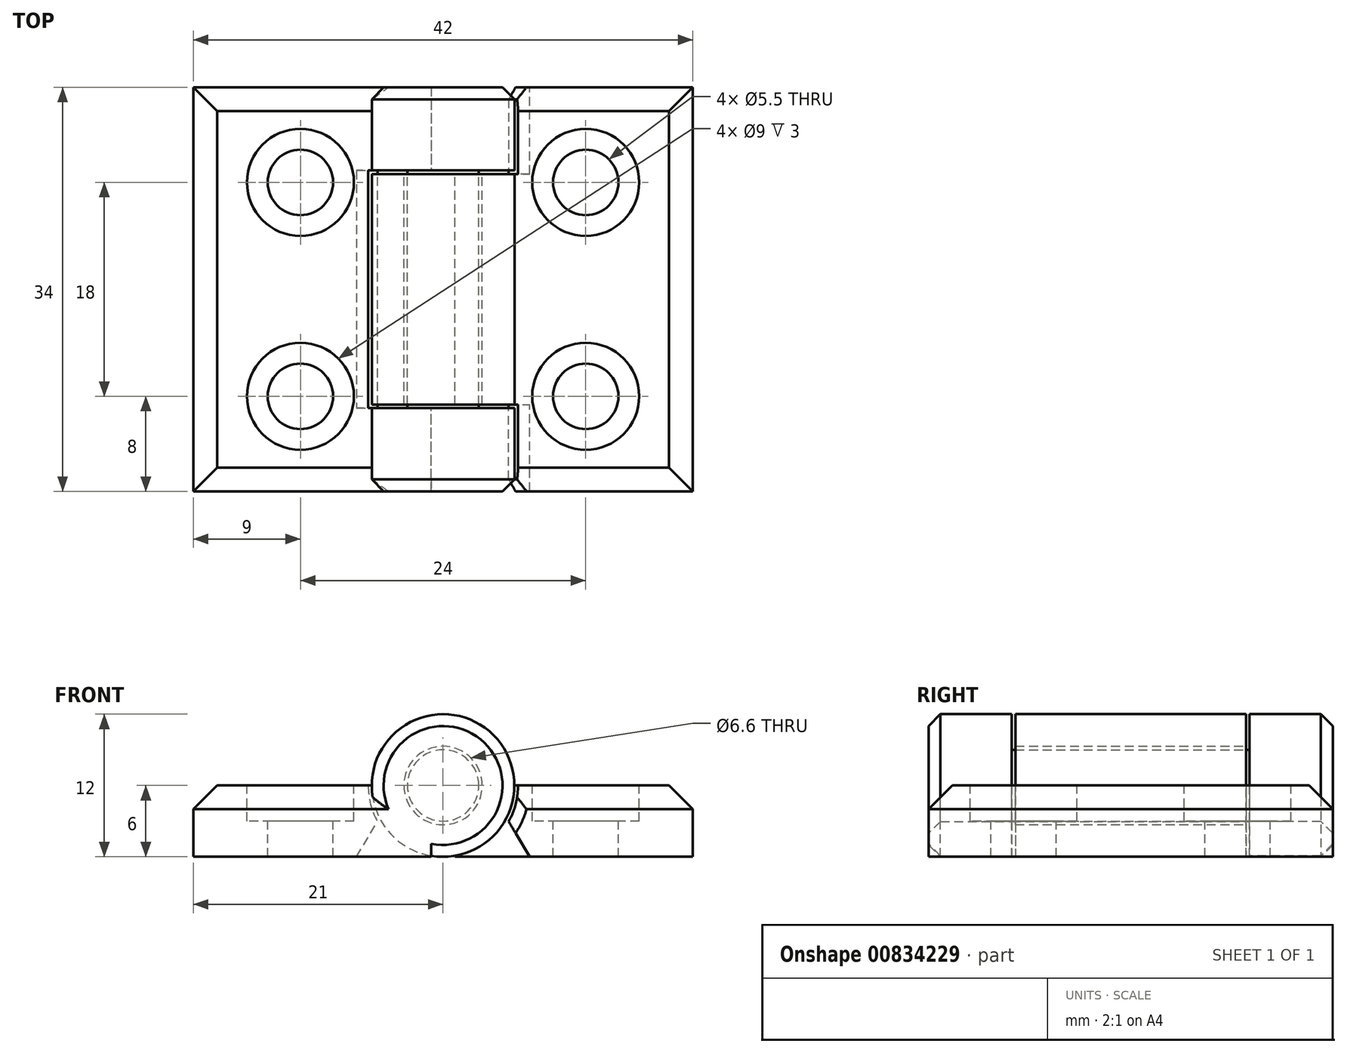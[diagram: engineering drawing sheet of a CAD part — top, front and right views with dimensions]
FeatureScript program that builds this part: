
annotation { "Feature Type Name" : "Feature", "Feature Type Description" : "" }
export const myFeature = defineFeature(function(context is Context, id is Id, definition is map)
    precondition{}
    {
        {
            var Q0;
            Q0=qCreatedBy(makeId("Front.planeOp"),FACE);
            var sketch = newSketch(context, id + "F0", { "sketchPlane" : qUnion([Q0])});
            skLineSegment(sketch, "E0.bottom", {"start": v(0, 0) * mm, "end": v(20, 0) * mm});
            skLineSegment(sketch, "E0.top", {"start": v(0, 6) * mm, "end": v(20, 6) * mm});
            skLineSegment(sketch, "E0.left", {"start": v(0, 0) * mm, "end": v(0, 6) * mm});
            skLineSegment(sketch, "E0.right", {"start": v(20, 0) * mm, "end": v(20, 6) * mm});
            skLineSegment(sketch, "E1.bottom", {"start": v(22, 6) * mm, "end": v(42, 6) * mm});
            skLineSegment(sketch, "E1.top", {"start": v(22, 0) * mm, "end": v(42, 0) * mm});
            skLineSegment(sketch, "E1.left", {"start": v(22, 6) * mm, "end": v(22, 0) * mm});
            skLineSegment(sketch, "E1.right", {"start": v(42, 6) * mm, "end": v(42, 0) * mm});
            skLineSegment(sketch, "E2", {"start": v(20, 6) * mm, "end": v(22, 6) * mm, "construction": true});
            skCircle(sketch, "E3", {"center": v(21, 6) * mm, "radius": 6 * mm});
            skCircle(sketch, "E4", {"center": v(21, 6) * mm, "radius": 3.3 * mm});
            skCircle(sketch, "E5", {"center": v(21, 6) * mm, "radius": 3 * mm});
            skCircle(sketch, "E6", {"center": v(21, 6) * mm, "radius": 6.3 * mm});
            skSolve(sketch);
        }
        {
            var Q0;
            {var subQ0=sQuery(id+"F0.wireOp",EDGE,"E0.left");Q0=makeQuery(id+"F0.imprint","IMPRINT",FACE,{"disambiguationData":[TD([[makeQuery(id+"F0.imprint","IMPRINT",EDGE,{"derivedFrom":subQ0}),-1.0]])]});}
            var Q1;
            {var subQ0=sQuery(id+"F0.wireOp",EDGE,"E1.right");Q1=makeQuery(id+"F0.imprint","IMPRINT",FACE,{"disambiguationData":[TD([[makeQuery(id+"F0.imprint","IMPRINT",EDGE,{"derivedFrom":subQ0}),-1.0]])]});}
            var Q2;
            {var subQ1=sQuery(id+"F0.wireOp",EDGE,"E1.bottom");var subQ7=sQuery(id+"F0.wireOp",EDGE,"E6");var subQ9=makeQuery(id+"F0.imprint","INTERSECT",VERTEX,{"derivedFrom":[subQ1,subQ7]});Q2=makeQuery(id+"F0.imprint","IMPRINT",FACE,{"disambiguationData":[TD([[makeQuery(id+"F0.imprint","IMPRINT",EDGE,{"disambiguationData":[TD([[subQ9,1.0]])],"derivedFrom":subQ1}),-1.0]])]});}
            var Q3;
            {var subQ0=sQuery(id+"F0.wireOp",EDGE,"E3");var subQ1=sQuery(id+"F0.wireOp",EDGE,"E0.top");var subQ2=makeQuery(id+"F0.imprint","INTERSECT",VERTEX,{"derivedFrom":[subQ1,subQ0]});Q3=makeQuery(id+"F0.imprint","IMPRINT",FACE,{"disambiguationData":[TD([[makeQuery(id+"F0.imprint","IMPRINT",EDGE,{"disambiguationData":[TD([[subQ2,-1.0]])],"derivedFrom":subQ1}),-1.0]])]});}
            var Q4;
            {var subQ0=sQuery(id+"F0.wireOp",EDGE,"E3");var subQ1=sQuery(id+"F0.wireOp",EDGE,"E0.right");var subQ2=makeQuery(id+"F0.imprint","INTERSECT",VERTEX,{"derivedFrom":[subQ1,subQ0]});Q4=makeQuery(id+"F0.imprint","IMPRINT",FACE,{"disambiguationData":[TD([[makeQuery(id+"F0.imprint","IMPRINT",EDGE,{"disambiguationData":[TD([[subQ2,-1.0]])],"derivedFrom":subQ1}),-1.0]])]});}
            var Q5;
            {var subQ0=sQuery(id+"F0.wireOp",EDGE,"E4");var subQ1=sQuery(id+"F0.wireOp",EDGE,"E1.bottom");var subQ2=makeQuery(id+"F0.imprint","INTERSECT",VERTEX,{"derivedFrom":[subQ1,subQ0]});Q5=makeQuery(id+"F0.imprint","IMPRINT",FACE,{"disambiguationData":[TD([[makeQuery(id+"F0.imprint","IMPRINT",EDGE,{"disambiguationData":[TD([[subQ2,-1.0]])],"derivedFrom":subQ1}),-1.0]])]});}
            var Q6;
            {var subQ0=sQuery(id+"F0.wireOp",EDGE,"E3");var subQ1=sQuery(id+"F0.wireOp",EDGE,"E0.top");var subQ2=makeQuery(id+"F0.imprint","INTERSECT",VERTEX,{"derivedFrom":[subQ1,subQ0]});Q6=makeQuery(id+"F0.imprint","IMPRINT",FACE,{"disambiguationData":[TD([[makeQuery(id+"F0.imprint","IMPRINT",EDGE,{"disambiguationData":[TD([[subQ2,-1.0]])],"derivedFrom":subQ1}),1.0]])]});}
            var Q7;
            {var subQ0=sQuery(id+"F0.wireOp",EDGE,"E0.right");var subQ1=sQuery(id+"F0.wireOp",EDGE,"E0.top");var subQ2=makeQuery(id+"F0.imprint","INTERSECT",VERTEX,{"derivedFrom":[subQ1,subQ0]});Q7=makeQuery(id+"F0.imprint","IMPRINT",FACE,{"disambiguationData":[TD([[makeQuery(id+"F0.imprint","IMPRINT",EDGE,{"disambiguationData":[TD([[subQ2,1.0]])],"derivedFrom":subQ1}),-1.0]])]});}
            var Q8;
            {var subQ6=sQuery(id+"F0.wireOp",EDGE,"E0.right");var subQ8=sQuery(id+"F0.wireOp",EDGE,"E0.top");var subQ9=makeQuery(id+"F0.imprint","INTERSECT",VERTEX,{"derivedFrom":[subQ8,subQ6]});Q8=makeQuery(id+"F0.imprint","IMPRINT",FACE,{"disambiguationData":[TD([[makeQuery(id+"F0.imprint","IMPRINT",EDGE,{"disambiguationData":[TD([[subQ9,1.0]])],"derivedFrom":subQ8}),1.0]])]});}
            var Q9;
            {var subQ0=sQuery(id+"F0.wireOp",EDGE,"E1.left");var subQ1=sQuery(id+"F0.wireOp",EDGE,"E1.bottom");var subQ2=makeQuery(id+"F0.imprint","INTERSECT",VERTEX,{"derivedFrom":[subQ1,subQ0]});Q9=makeQuery(id+"F0.imprint","IMPRINT",FACE,{"disambiguationData":[TD([[makeQuery(id+"F0.imprint","IMPRINT",EDGE,{"disambiguationData":[TD([[subQ2,-1.0]])],"derivedFrom":subQ1}),-1.0]])]});}
            extrude(context, id + "F1", {"entities" : qUnion([Q0, Q1, Q2, Q3, Q4, Q5, Q6, Q7, Q8, Q9]), "endBound" : BoundingType.SYMMETRIC, "depth" : 19.4 * mm, "offsetDistance" : 25 * mm});
        }
        {
            var Q0;
            Q0=makeQuery(id+"F1.opExtrude","CAP_FACE",FACE,{"disambiguationData":[OSD([sQuery(id+"F0.wireOp",EDGE,"E0.bottom"),sQuery(id+"F0.wireOp",EDGE,"E0.top"),sQuery(id+"F0.wireOp",EDGE,"E0.left"),sQuery(id+"F0.wireOp",EDGE,"E6")])],"isStart":false});
            var sketch = newSketch(context, id + "F2", { "sketchPlane" : qUnion([Q0])});
            skLineSegment(sketch, "E7.bottom", {"start": v(0, 0) * mm, "end": v(20, 0) * mm});
            skLineSegment(sketch, "E7.top", {"start": v(0, 6) * mm, "end": v(20, 6) * mm});
            skLineSegment(sketch, "E7.left", {"start": v(0, 0) * mm, "end": v(0, 6) * mm});
            skLineSegment(sketch, "E7.right", {"start": v(20, 0) * mm, "end": v(20, 6) * mm});
            skLineSegment(sketch, "E8.bottom", {"start": v(22, 6) * mm, "end": v(42, 6) * mm});
            skLineSegment(sketch, "E8.top", {"start": v(22, 0) * mm, "end": v(42, 0) * mm});
            skLineSegment(sketch, "E8.left", {"start": v(22, 6) * mm, "end": v(22, 0) * mm});
            skLineSegment(sketch, "E8.right", {"start": v(42, 6) * mm, "end": v(42, 0) * mm});
            skLineSegment(sketch, "E9", {"start": v(20, 6) * mm, "end": v(22, 6) * mm, "construction": true});
            skCircle(sketch, "E10", {"center": v(21, 6) * mm, "radius": 6 * mm});
            skCircle(sketch, "E11", {"center": v(21, 6) * mm, "radius": 3.3 * mm});
            skCircle(sketch, "E12", {"center": v(21, 6) * mm, "radius": 3 * mm});
            skCircle(sketch, "E13", {"center": v(21, 6) * mm, "radius": 6.3 * mm});
            skSolve(sketch);
        }
        {
            var Q0;
            {var subQ0=sQuery(id+"F2.wireOp",EDGE,"E7.left");Q0=makeQuery(id+"F2.imprint","IMPRINT",FACE,{"disambiguationData":[TD([[makeQuery(id+"F2.imprint","IMPRINT",EDGE,{"derivedFrom":subQ0}),-1.0]])]});}
            var Q1;
            {var subQ6=sQuery(id+"F2.wireOp",EDGE,"E7.right");var subQ8=sQuery(id+"F2.wireOp",EDGE,"E7.top");var subQ9=makeQuery(id+"F2.imprint","INTERSECT",VERTEX,{"derivedFrom":[subQ8,subQ6]});Q1=makeQuery(id+"F2.imprint","IMPRINT",FACE,{"disambiguationData":[TD([[makeQuery(id+"F2.imprint","IMPRINT",EDGE,{"disambiguationData":[TD([[subQ9,1.0]])],"derivedFrom":subQ8}),1.0]])]});}
            var Q2;
            {var subQ0=sQuery(id+"F2.wireOp",EDGE,"E7.right");var subQ1=sQuery(id+"F2.wireOp",EDGE,"E7.top");var subQ2=makeQuery(id+"F2.imprint","INTERSECT",VERTEX,{"derivedFrom":[subQ1,subQ0]});Q2=makeQuery(id+"F2.imprint","IMPRINT",FACE,{"disambiguationData":[TD([[makeQuery(id+"F2.imprint","IMPRINT",EDGE,{"disambiguationData":[TD([[subQ2,1.0]])],"derivedFrom":subQ1}),-1.0]])]});}
            var Q3;
            {var subQ0=sQuery(id+"F2.wireOp",EDGE,"E8.left");var subQ1=sQuery(id+"F2.wireOp",EDGE,"E8.bottom");var subQ2=makeQuery(id+"F2.imprint","INTERSECT",VERTEX,{"derivedFrom":[subQ1,subQ0]});Q3=makeQuery(id+"F2.imprint","IMPRINT",FACE,{"disambiguationData":[TD([[makeQuery(id+"F2.imprint","IMPRINT",EDGE,{"disambiguationData":[TD([[subQ2,-1.0]])],"derivedFrom":subQ1}),-1.0]])]});}
            var Q4;
            {var subQ0=sQuery(id+"F2.wireOp",EDGE,"E8.right");Q4=makeQuery(id+"F2.imprint","IMPRINT",FACE,{"disambiguationData":[TD([[makeQuery(id+"F2.imprint","IMPRINT",EDGE,{"derivedFrom":subQ0}),-1.0]])]});}
            extrude(context, id + "F3", {"entities" : qUnion([Q0, Q1, Q2, Q3, Q4]), "depth" : .3 * mm, "offsetDistance" : 25 * mm});
        }
        {
            var Q0;
            Q0=makeQuery(id+"F1.opExtrude","CAP_FACE",FACE,{"disambiguationData":[OSD([sQuery(id+"F0.wireOp",EDGE,"E1.bottom"),sQuery(id+"F0.wireOp",EDGE,"E1.top"),sQuery(id+"F0.wireOp",EDGE,"E1.left"),sQuery(id+"F0.wireOp",EDGE,"E1.right"),sQuery(id+"F0.wireOp",EDGE,"E3"),sQuery(id+"F0.wireOp",EDGE,"E4")])],"isStart":true});
            var sketch = newSketch(context, id + "F4", { "sketchPlane" : qUnion([Q0])});
            skLineSegment(sketch, "E14.bottom", {"start": v(-42, 0) * mm, "end": v(-22, 0) * mm});
            skLineSegment(sketch, "E14.top", {"start": v(-42, 6) * mm, "end": v(-22, 6) * mm});
            skLineSegment(sketch, "E14.left", {"start": v(-42, 0) * mm, "end": v(-42, 6) * mm});
            skLineSegment(sketch, "E14.right", {"start": v(-22, 0) * mm, "end": v(-22, 6) * mm});
            skLineSegment(sketch, "E15.bottom", {"start": v(-20, 6) * mm, "end": v(0, 6) * mm});
            skLineSegment(sketch, "E15.top", {"start": v(-20, 0) * mm, "end": v(0, 0) * mm});
            skLineSegment(sketch, "E15.left", {"start": v(-20, 6) * mm, "end": v(-20, 0) * mm});
            skLineSegment(sketch, "E15.right", {"start": v(0, 6) * mm, "end": v(0, 0) * mm});
            skLineSegment(sketch, "E16", {"start": v(-22, 6) * mm, "end": v(-20, 6) * mm, "construction": true});
            skCircle(sketch, "E17", {"center": v(-21, 6) * mm, "radius": 6 * mm});
            skCircle(sketch, "E18", {"center": v(-21, 6) * mm, "radius": 3.3 * mm});
            skCircle(sketch, "E19", {"center": v(-21, 6) * mm, "radius": 3 * mm});
            skCircle(sketch, "E20", {"center": v(-21, 6) * mm, "radius": 6.3 * mm});
            skSolve(sketch);
        }
        {
            var Q0;
            {var subQ0=sQuery(id+"F4.wireOp",EDGE,"E15.right");Q0=makeQuery(id+"F4.imprint","IMPRINT",FACE,{"disambiguationData":[TD([[makeQuery(id+"F4.imprint","IMPRINT",EDGE,{"derivedFrom":subQ0}),-1.0]])]});}
            var Q1;
            {var subQ0=sQuery(id+"F4.wireOp",EDGE,"E14.left");Q1=makeQuery(id+"F4.imprint","IMPRINT",FACE,{"disambiguationData":[TD([[makeQuery(id+"F4.imprint","IMPRINT",EDGE,{"derivedFrom":subQ0}),1.0]])]});}
            var Q2;
            {var subQ6=sQuery(id+"F4.wireOp",EDGE,"E14.right");var subQ8=sQuery(id+"F4.wireOp",EDGE,"E14.top");var subQ9=makeQuery(id+"F4.imprint","INTERSECT",VERTEX,{"derivedFrom":[subQ8,subQ6]});Q2=makeQuery(id+"F4.imprint","IMPRINT",FACE,{"disambiguationData":[TD([[makeQuery(id+"F4.imprint","IMPRINT",EDGE,{"disambiguationData":[TD([[subQ9,1.0]])],"derivedFrom":subQ8}),1.0]])]});}
            var Q3;
            {var subQ0=sQuery(id+"F4.wireOp",EDGE,"E14.right");var subQ1=sQuery(id+"F4.wireOp",EDGE,"E14.top");var subQ2=makeQuery(id+"F4.imprint","INTERSECT",VERTEX,{"derivedFrom":[subQ1,subQ0]});Q3=makeQuery(id+"F4.imprint","IMPRINT",FACE,{"disambiguationData":[TD([[makeQuery(id+"F4.imprint","IMPRINT",EDGE,{"disambiguationData":[TD([[subQ2,1.0]])],"derivedFrom":subQ1}),-1.0]])]});}
            var Q4;
            {var subQ0=sQuery(id+"F4.wireOp",EDGE,"E15.left");var subQ1=sQuery(id+"F4.wireOp",EDGE,"E15.bottom");var subQ2=makeQuery(id+"F4.imprint","INTERSECT",VERTEX,{"derivedFrom":[subQ1,subQ0]});Q4=makeQuery(id+"F4.imprint","IMPRINT",FACE,{"disambiguationData":[TD([[makeQuery(id+"F4.imprint","IMPRINT",EDGE,{"disambiguationData":[TD([[subQ2,-1.0]])],"derivedFrom":subQ1}),-1.0]])]});}
            extrude(context, id + "F5", {"entities" : qUnion([Q0, Q1, Q2, Q3, Q4]), "depth" : .3 * mm, "offsetDistance" : 25 * mm});
        }
        {
            var Q0;
            Q0=makeQuery(id+"F5.opExtrude","CAP_FACE",FACE,{"disambiguationData":[OSD([sQuery(id+"F4.wireOp",EDGE,"E14.bottom"),sQuery(id+"F4.wireOp",EDGE,"E14.top"),sQuery(id+"F4.wireOp",EDGE,"E14.left"),sQuery(id+"F4.wireOp",EDGE,"E20")])],"isStart":false});
            var sketch = newSketch(context, id + "F6", { "sketchPlane" : qUnion([Q0])});
            skLineSegment(sketch, "E21.bottom", {"start": v(-42, 0) * mm, "end": v(-22, 0) * mm});
            skLineSegment(sketch, "E21.top", {"start": v(-42, 6) * mm, "end": v(-22, 6) * mm});
            skLineSegment(sketch, "E21.left", {"start": v(-42, 0) * mm, "end": v(-42, 6) * mm});
            skLineSegment(sketch, "E21.right", {"start": v(-22, 0) * mm, "end": v(-22, 6) * mm});
            skLineSegment(sketch, "E22.bottom", {"start": v(-20, 6) * mm, "end": v(0, 6) * mm});
            skLineSegment(sketch, "E22.top", {"start": v(-20, 0) * mm, "end": v(0, 0) * mm});
            skLineSegment(sketch, "E22.left", {"start": v(-20, 6) * mm, "end": v(-20, 0) * mm});
            skLineSegment(sketch, "E22.right", {"start": v(0, 6) * mm, "end": v(0, 0) * mm});
            skLineSegment(sketch, "E23", {"start": v(-22, 6) * mm, "end": v(-20, 6) * mm, "construction": true});
            skCircle(sketch, "E24", {"center": v(-21, 6) * mm, "radius": 6 * mm});
            skCircle(sketch, "E25", {"center": v(-21, 6) * mm, "radius": 3.3 * mm});
            skCircle(sketch, "E26", {"center": v(-21, 6) * mm, "radius": 3 * mm});
            skCircle(sketch, "E27", {"center": v(-21, 6) * mm, "radius": 6.3 * mm});
            skSolve(sketch);
        }
        {
            var Q0;
            {var subQ0=sQuery(id+"F6.wireOp",EDGE,"E24");var subQ1=sQuery(id+"F6.wireOp",EDGE,"E21.top");var subQ2=makeQuery(id+"F6.imprint","INTERSECT",VERTEX,{"derivedFrom":[subQ1,subQ0]});Q0=makeQuery(id+"F6.imprint","IMPRINT",FACE,{"disambiguationData":[TD([[makeQuery(id+"F6.imprint","IMPRINT",EDGE,{"disambiguationData":[TD([[subQ2,-1.0]])],"derivedFrom":subQ1}),-1.0]])]});}
            var Q1;
            {var subQ0=sQuery(id+"F6.wireOp",EDGE,"E24");var subQ1=sQuery(id+"F6.wireOp",EDGE,"E21.right");var subQ2=makeQuery(id+"F6.imprint","INTERSECT",VERTEX,{"derivedFrom":[subQ1,subQ0]});Q1=makeQuery(id+"F6.imprint","IMPRINT",FACE,{"disambiguationData":[TD([[makeQuery(id+"F6.imprint","IMPRINT",EDGE,{"disambiguationData":[TD([[subQ2,-1.0]])],"derivedFrom":subQ1}),-1.0]])]});}
            var Q2;
            {var subQ0=sQuery(id+"F6.wireOp",EDGE,"E25");var subQ1=sQuery(id+"F6.wireOp",EDGE,"E22.bottom");var subQ2=makeQuery(id+"F6.imprint","INTERSECT",VERTEX,{"derivedFrom":[subQ1,subQ0]});Q2=makeQuery(id+"F6.imprint","IMPRINT",FACE,{"disambiguationData":[TD([[makeQuery(id+"F6.imprint","IMPRINT",EDGE,{"disambiguationData":[TD([[subQ2,-1.0]])],"derivedFrom":subQ1}),-1.0]])]});}
            var Q3;
            {var subQ0=sQuery(id+"F6.wireOp",EDGE,"E24");var subQ1=sQuery(id+"F6.wireOp",EDGE,"E21.top");var subQ2=makeQuery(id+"F6.imprint","INTERSECT",VERTEX,{"derivedFrom":[subQ1,subQ0]});Q3=makeQuery(id+"F6.imprint","IMPRINT",FACE,{"disambiguationData":[TD([[makeQuery(id+"F6.imprint","IMPRINT",EDGE,{"disambiguationData":[TD([[subQ2,-1.0]])],"derivedFrom":subQ1}),1.0]])]});}
            var Q4;
            {var subQ1=sQuery(id+"F6.wireOp",EDGE,"E22.bottom");var subQ7=sQuery(id+"F6.wireOp",EDGE,"E27");var subQ9=makeQuery(id+"F6.imprint","INTERSECT",VERTEX,{"derivedFrom":[subQ1,subQ7]});Q4=makeQuery(id+"F6.imprint","IMPRINT",FACE,{"disambiguationData":[TD([[makeQuery(id+"F6.imprint","IMPRINT",EDGE,{"disambiguationData":[TD([[subQ9,1.0]])],"derivedFrom":subQ1}),-1.0]])]});}
            var Q5;
            {var subQ0=sQuery(id+"F6.wireOp",EDGE,"E22.right");Q5=makeQuery(id+"F6.imprint","IMPRINT",FACE,{"disambiguationData":[TD([[makeQuery(id+"F6.imprint","IMPRINT",EDGE,{"derivedFrom":subQ0}),-1.0]])]});}
            var Q6;
            {var subQ0=sQuery(id+"F6.wireOp",EDGE,"E22.left");var subQ1=sQuery(id+"F6.wireOp",EDGE,"E22.bottom");var subQ2=makeQuery(id+"F6.imprint","INTERSECT",VERTEX,{"derivedFrom":[subQ1,subQ0]});Q6=makeQuery(id+"F6.imprint","IMPRINT",FACE,{"disambiguationData":[TD([[makeQuery(id+"F6.imprint","IMPRINT",EDGE,{"disambiguationData":[TD([[subQ2,-1.0]])],"derivedFrom":subQ1}),-1.0]])]});}
            var Q7;
            {var subQ6=sQuery(id+"F6.wireOp",EDGE,"E21.right");var subQ8=sQuery(id+"F6.wireOp",EDGE,"E21.top");var subQ9=makeQuery(id+"F6.imprint","INTERSECT",VERTEX,{"derivedFrom":[subQ8,subQ6]});Q7=makeQuery(id+"F6.imprint","IMPRINT",FACE,{"disambiguationData":[TD([[makeQuery(id+"F6.imprint","IMPRINT",EDGE,{"disambiguationData":[TD([[subQ9,1.0]])],"derivedFrom":subQ8}),1.0]])]});}
            var Q8;
            {var subQ0=sQuery(id+"F6.wireOp",EDGE,"E21.right");var subQ1=sQuery(id+"F6.wireOp",EDGE,"E21.top");var subQ2=makeQuery(id+"F6.imprint","INTERSECT",VERTEX,{"derivedFrom":[subQ1,subQ0]});Q8=makeQuery(id+"F6.imprint","IMPRINT",FACE,{"disambiguationData":[TD([[makeQuery(id+"F6.imprint","IMPRINT",EDGE,{"disambiguationData":[TD([[subQ2,1.0]])],"derivedFrom":subQ1}),-1.0]])]});}
            var Q9;
            {var subQ0=sQuery(id+"F6.wireOp",EDGE,"E21.left");Q9=makeQuery(id+"F6.imprint","IMPRINT",FACE,{"disambiguationData":[TD([[makeQuery(id+"F6.imprint","IMPRINT",EDGE,{"derivedFrom":subQ0}),1.0]])]});}
            var Q10;
            {var subQ0=sQuery(id+"F6.wireOp",EDGE,"E25");var subQ1=sQuery(id+"F6.wireOp",EDGE,"E21.right");var subQ2=makeQuery(id+"F6.imprint","INTERSECT",VERTEX,{"derivedFrom":[subQ1,subQ0]});Q10=makeQuery(id+"F6.imprint","IMPRINT",FACE,{"disambiguationData":[TD([[makeQuery(id+"F6.imprint","IMPRINT",EDGE,{"disambiguationData":[TD([[subQ2,-1.0]])],"derivedFrom":subQ1}),-1.0]])]});}
            var Q11;
            {var subQ0=sQuery(id+"F6.wireOp",EDGE,"E25");var subQ1=sQuery(id+"F6.wireOp",EDGE,"E21.top");var subQ2=makeQuery(id+"F6.imprint","INTERSECT",VERTEX,{"derivedFrom":[subQ1,subQ0]});Q11=makeQuery(id+"F6.imprint","IMPRINT",FACE,{"disambiguationData":[TD([[makeQuery(id+"F6.imprint","IMPRINT",EDGE,{"disambiguationData":[TD([[subQ2,-1.0]])],"derivedFrom":subQ1}),-1.0]])]});}
            var Q12;
            {var subQ0=sQuery(id+"F6.wireOp",EDGE,"E25");var subQ1=sQuery(id+"F6.wireOp",EDGE,"E21.top");var subQ2=makeQuery(id+"F6.imprint","INTERSECT",VERTEX,{"derivedFrom":[subQ1,subQ0]});Q12=makeQuery(id+"F6.imprint","IMPRINT",FACE,{"disambiguationData":[TD([[makeQuery(id+"F6.imprint","IMPRINT",EDGE,{"disambiguationData":[TD([[subQ2,-1.0]])],"derivedFrom":subQ1}),1.0]])]});}
            var Q13;
            {var subQ0=sQuery(id+"F6.wireOp",EDGE,"E26");var subQ1=sQuery(id+"F6.wireOp",EDGE,"E22.bottom");var subQ2=makeQuery(id+"F6.imprint","INTERSECT",VERTEX,{"derivedFrom":[subQ1,subQ0]});Q13=makeQuery(id+"F6.imprint","IMPRINT",FACE,{"disambiguationData":[TD([[makeQuery(id+"F6.imprint","IMPRINT",EDGE,{"disambiguationData":[TD([[subQ2,-1.0]])],"derivedFrom":subQ1}),-1.0]])]});}
            extrude(context, id + "F7", {"entities" : qUnion([Q0, Q1, Q2, Q3, Q4, Q5, Q6, Q7, Q8, Q9, Q10, Q11, Q12, Q13]), "depth" : 7 * mm, "offsetDistance" : 25 * mm});
        }
        {
            var Q0;
            Q0=makeQuery(id+"F3.opExtrude","CAP_FACE",FACE,{"disambiguationData":[OSD([sQuery(id+"F2.wireOp",EDGE,"E7.bottom"),sQuery(id+"F2.wireOp",EDGE,"E7.top"),sQuery(id+"F2.wireOp",EDGE,"E7.left"),sQuery(id+"F2.wireOp",EDGE,"E13")])],"isStart":false});
            var sketch = newSketch(context, id + "F8", { "sketchPlane" : qUnion([Q0])});
            skLineSegment(sketch, "E28.bottom", {"start": v(0, 0) * mm, "end": v(20, 0) * mm});
            skLineSegment(sketch, "E28.top", {"start": v(0, 6) * mm, "end": v(20, 6) * mm});
            skLineSegment(sketch, "E28.left", {"start": v(0, 0) * mm, "end": v(0, 6) * mm});
            skLineSegment(sketch, "E28.right", {"start": v(20, 0) * mm, "end": v(20, 6) * mm});
            skLineSegment(sketch, "E29.bottom", {"start": v(22, 6) * mm, "end": v(42, 6) * mm});
            skLineSegment(sketch, "E29.top", {"start": v(22, 0) * mm, "end": v(42, 0) * mm});
            skLineSegment(sketch, "E29.left", {"start": v(22, 6) * mm, "end": v(22, 0) * mm});
            skLineSegment(sketch, "E29.right", {"start": v(42, 6) * mm, "end": v(42, 0) * mm});
            skLineSegment(sketch, "E30", {"start": v(20, 6) * mm, "end": v(22, 6) * mm, "construction": true});
            skCircle(sketch, "E31", {"center": v(21, 6) * mm, "radius": 6 * mm});
            skCircle(sketch, "E32", {"center": v(21, 6) * mm, "radius": 3.3 * mm});
            skCircle(sketch, "E33", {"center": v(21, 6) * mm, "radius": 3 * mm});
            skCircle(sketch, "E34", {"center": v(21, 6) * mm, "radius": 6.3 * mm});
            skSolve(sketch);
        }
        {
            var Q0;
            {var subQ0=sQuery(id+"F8.wireOp",EDGE,"E29.right");Q0=makeQuery(id+"F8.imprint","IMPRINT",FACE,{"disambiguationData":[TD([[makeQuery(id+"F8.imprint","IMPRINT",EDGE,{"derivedFrom":subQ0}),-1.0]])]});}
            var Q1;
            {var subQ6=sQuery(id+"F8.wireOp",EDGE,"E28.right");var subQ8=sQuery(id+"F8.wireOp",EDGE,"E28.top");var subQ9=makeQuery(id+"F8.imprint","INTERSECT",VERTEX,{"derivedFrom":[subQ8,subQ6]});Q1=makeQuery(id+"F8.imprint","IMPRINT",FACE,{"disambiguationData":[TD([[makeQuery(id+"F8.imprint","IMPRINT",EDGE,{"disambiguationData":[TD([[subQ9,1.0]])],"derivedFrom":subQ8}),1.0]])]});}
            var Q2;
            {var subQ0=sQuery(id+"F8.wireOp",EDGE,"E29.left");var subQ1=sQuery(id+"F8.wireOp",EDGE,"E29.bottom");var subQ2=makeQuery(id+"F8.imprint","INTERSECT",VERTEX,{"derivedFrom":[subQ1,subQ0]});Q2=makeQuery(id+"F8.imprint","IMPRINT",FACE,{"disambiguationData":[TD([[makeQuery(id+"F8.imprint","IMPRINT",EDGE,{"disambiguationData":[TD([[subQ2,-1.0]])],"derivedFrom":subQ1}),-1.0]])]});}
            var Q3;
            {var subQ0=sQuery(id+"F8.wireOp",EDGE,"E28.right");var subQ1=sQuery(id+"F8.wireOp",EDGE,"E28.top");var subQ2=makeQuery(id+"F8.imprint","INTERSECT",VERTEX,{"derivedFrom":[subQ1,subQ0]});Q3=makeQuery(id+"F8.imprint","IMPRINT",FACE,{"disambiguationData":[TD([[makeQuery(id+"F8.imprint","IMPRINT",EDGE,{"disambiguationData":[TD([[subQ2,1.0]])],"derivedFrom":subQ1}),-1.0]])]});}
            var Q4;
            {var subQ0=sQuery(id+"F8.wireOp",EDGE,"E31");var subQ1=sQuery(id+"F8.wireOp",EDGE,"E28.top");var subQ2=makeQuery(id+"F8.imprint","INTERSECT",VERTEX,{"derivedFrom":[subQ1,subQ0]});Q4=makeQuery(id+"F8.imprint","IMPRINT",FACE,{"disambiguationData":[TD([[makeQuery(id+"F8.imprint","IMPRINT",EDGE,{"disambiguationData":[TD([[subQ2,-1.0]])],"derivedFrom":subQ1}),1.0]])]});}
            var Q5;
            {var subQ0=sQuery(id+"F8.wireOp",EDGE,"E31");var subQ1=sQuery(id+"F8.wireOp",EDGE,"E28.top");var subQ2=makeQuery(id+"F8.imprint","INTERSECT",VERTEX,{"derivedFrom":[subQ1,subQ0]});Q5=makeQuery(id+"F8.imprint","IMPRINT",FACE,{"disambiguationData":[TD([[makeQuery(id+"F8.imprint","IMPRINT",EDGE,{"disambiguationData":[TD([[subQ2,-1.0]])],"derivedFrom":subQ1}),-1.0]])]});}
            var Q6;
            {var subQ0=sQuery(id+"F8.wireOp",EDGE,"E31");var subQ1=sQuery(id+"F8.wireOp",EDGE,"E28.right");var subQ2=makeQuery(id+"F8.imprint","INTERSECT",VERTEX,{"derivedFrom":[subQ1,subQ0]});Q6=makeQuery(id+"F8.imprint","IMPRINT",FACE,{"disambiguationData":[TD([[makeQuery(id+"F8.imprint","IMPRINT",EDGE,{"disambiguationData":[TD([[subQ2,-1.0]])],"derivedFrom":subQ1}),-1.0]])]});}
            var Q7;
            {var subQ0=sQuery(id+"F8.wireOp",EDGE,"E32");var subQ1=sQuery(id+"F8.wireOp",EDGE,"E29.bottom");var subQ2=makeQuery(id+"F8.imprint","INTERSECT",VERTEX,{"derivedFrom":[subQ1,subQ0]});Q7=makeQuery(id+"F8.imprint","IMPRINT",FACE,{"disambiguationData":[TD([[makeQuery(id+"F8.imprint","IMPRINT",EDGE,{"disambiguationData":[TD([[subQ2,-1.0]])],"derivedFrom":subQ1}),-1.0]])]});}
            var Q8;
            {var subQ5=sQuery(id+"F8.wireOp",EDGE,"E34");var subQ7=sQuery(id+"F8.wireOp",EDGE,"E28.bottom");var subQ9=makeQuery(id+"F8.imprint","INTERSECT",VERTEX,{"derivedFrom":[subQ7,subQ5]});Q8=makeQuery(id+"F8.imprint","IMPRINT",FACE,{"disambiguationData":[TD([[makeQuery(id+"F8.imprint","IMPRINT",EDGE,{"disambiguationData":[TD([[subQ9,-1.0]])],"derivedFrom":subQ7}),1.0]])]});}
            var Q9;
            {var subQ0=sQuery(id+"F8.wireOp",EDGE,"E28.left");Q9=makeQuery(id+"F8.imprint","IMPRINT",FACE,{"disambiguationData":[TD([[makeQuery(id+"F8.imprint","IMPRINT",EDGE,{"derivedFrom":subQ0}),-1.0]])]});}
            var Q10;
            {var subQ0=sQuery(id+"F8.wireOp",EDGE,"E32");var subQ1=sQuery(id+"F8.wireOp",EDGE,"E28.top");var subQ2=makeQuery(id+"F8.imprint","INTERSECT",VERTEX,{"derivedFrom":[subQ1,subQ0]});Q10=makeQuery(id+"F8.imprint","IMPRINT",FACE,{"disambiguationData":[TD([[makeQuery(id+"F8.imprint","IMPRINT",EDGE,{"disambiguationData":[TD([[subQ2,-1.0]])],"derivedFrom":subQ1}),1.0]])]});}
            var Q11;
            {var subQ0=sQuery(id+"F8.wireOp",EDGE,"E32");var subQ1=sQuery(id+"F8.wireOp",EDGE,"E28.top");var subQ2=makeQuery(id+"F8.imprint","INTERSECT",VERTEX,{"derivedFrom":[subQ1,subQ0]});Q11=makeQuery(id+"F8.imprint","IMPRINT",FACE,{"disambiguationData":[TD([[makeQuery(id+"F8.imprint","IMPRINT",EDGE,{"disambiguationData":[TD([[subQ2,-1.0]])],"derivedFrom":subQ1}),-1.0]])]});}
            var Q12;
            {var subQ0=sQuery(id+"F8.wireOp",EDGE,"E32");var subQ1=sQuery(id+"F8.wireOp",EDGE,"E28.right");var subQ2=makeQuery(id+"F8.imprint","INTERSECT",VERTEX,{"derivedFrom":[subQ1,subQ0]});Q12=makeQuery(id+"F8.imprint","IMPRINT",FACE,{"disambiguationData":[TD([[makeQuery(id+"F8.imprint","IMPRINT",EDGE,{"disambiguationData":[TD([[subQ2,-1.0]])],"derivedFrom":subQ1}),-1.0]])]});}
            var Q13;
            {var subQ0=sQuery(id+"F8.wireOp",EDGE,"E33");var subQ1=sQuery(id+"F8.wireOp",EDGE,"E29.bottom");var subQ2=makeQuery(id+"F8.imprint","INTERSECT",VERTEX,{"derivedFrom":[subQ1,subQ0]});Q13=makeQuery(id+"F8.imprint","IMPRINT",FACE,{"disambiguationData":[TD([[makeQuery(id+"F8.imprint","IMPRINT",EDGE,{"disambiguationData":[TD([[subQ2,-1.0]])],"derivedFrom":subQ1}),-1.0]])]});}
            extrude(context, id + "F9", {"entities" : qUnion([Q0, Q1, Q2, Q3, Q4, Q5, Q6, Q7, Q8, Q9, Q10, Q11, Q12, Q13]), "depth" : 7 * mm, "offsetDistance" : 25 * mm});
        }
        {
            var Q0;
            Q0=makeQuery(id+"F9.opExtrude","SWEPT_BODY",BODY,{"disambiguationData":[OSD([sQuery(id+"F8.wireOp",EDGE,"E28.bottom"),sQuery(id+"F8.wireOp",EDGE,"E28.top"),sQuery(id+"F8.wireOp",EDGE,"E28.left"),sQuery(id+"F8.wireOp",EDGE,"E28.right"),sQuery(id+"F8.wireOp",EDGE,"E31")])]});
            var Q1;
            Q1=makeQuery(id+"F5.opExtrude","SWEPT_BODY",BODY,{"disambiguationData":[OSD([sQuery(id+"F4.wireOp",EDGE,"E15.bottom"),sQuery(id+"F4.wireOp",EDGE,"E15.top"),sQuery(id+"F4.wireOp",EDGE,"E15.right"),sQuery(id+"F4.wireOp",EDGE,"E20")])]});
            var Q2;
            Q2=makeQuery(id+"F7.opExtrude","SWEPT_BODY",BODY,{"disambiguationData":[OSD([sQuery(id+"F6.wireOp",EDGE,"E22.bottom"),sQuery(id+"F6.wireOp",EDGE,"E22.top"),sQuery(id+"F6.wireOp",EDGE,"E22.left"),sQuery(id+"F6.wireOp",EDGE,"E22.right"),sQuery(id+"F6.wireOp",EDGE,"E24")])]});
            booleanBodies(context, id + "F10", {"operationType" : BooleanOperationType.UNION, "tools" : qUnion([Q0, Q1, Q2])});
        }
        {
            var Q0;
            Q0=makeQuery(id+"F1.opExtrude","SWEPT_BODY",BODY,{"disambiguationData":[OSD([sQuery(id+"F0.wireOp",EDGE,"E0.bottom"),sQuery(id+"F0.wireOp",EDGE,"E0.top"),sQuery(id+"F0.wireOp",EDGE,"E0.left"),sQuery(id+"F0.wireOp",EDGE,"E6")])]});
            var Q1;
            Q1=makeQuery(id+"F5.opExtrude","SWEPT_BODY",BODY,{"disambiguationData":[OSD([sQuery(id+"F4.wireOp",EDGE,"E15.bottom"),sQuery(id+"F4.wireOp",EDGE,"E15.top"),sQuery(id+"F4.wireOp",EDGE,"E15.right"),sQuery(id+"F4.wireOp",EDGE,"E20")])]});
            booleanBodies(context, id + "F11", {"operationType" : BooleanOperationType.UNION, "tools" : qUnion([Q0, Q1])});
        }
        {
            var Q0;
            Q0=makeQuery(id+"F1.opExtrude","SWEPT_BODY",BODY,{"disambiguationData":[OSD([sQuery(id+"F0.wireOp",EDGE,"E0.bottom"),sQuery(id+"F0.wireOp",EDGE,"E0.top"),sQuery(id+"F0.wireOp",EDGE,"E0.left"),sQuery(id+"F0.wireOp",EDGE,"E6")])]});
            var Q1;
            Q1=makeQuery(id+"F3.opExtrude","SWEPT_BODY",BODY,{"disambiguationData":[OSD([sQuery(id+"F2.wireOp",EDGE,"E7.bottom"),sQuery(id+"F2.wireOp",EDGE,"E7.top"),sQuery(id+"F2.wireOp",EDGE,"E7.left"),sQuery(id+"F2.wireOp",EDGE,"E13")])]});
            booleanBodies(context, id + "F12", {"operationType" : BooleanOperationType.UNION, "tools" : qUnion([Q0, Q1])});
        }
        {
            var Q0;
            Q0=makeQuery(id+"F1.opExtrude","SWEPT_BODY",BODY,{"disambiguationData":[OSD([sQuery(id+"F0.wireOp",EDGE,"E0.bottom"),sQuery(id+"F0.wireOp",EDGE,"E0.top"),sQuery(id+"F0.wireOp",EDGE,"E0.left"),sQuery(id+"F0.wireOp",EDGE,"E6")])]});
            var Q1;
            Q1=makeQuery(id+"F9.opExtrude","SWEPT_BODY",BODY,{"disambiguationData":[OSD([sQuery(id+"F8.wireOp",EDGE,"E28.bottom"),sQuery(id+"F8.wireOp",EDGE,"E28.top"),sQuery(id+"F8.wireOp",EDGE,"E28.left"),sQuery(id+"F8.wireOp",EDGE,"E28.right"),sQuery(id+"F8.wireOp",EDGE,"E31")])]});
            booleanBodies(context, id + "F13", {"operationType" : BooleanOperationType.UNION, "tools" : qUnion([Q0, Q1])});
        }
        {
            var Q0;
            Q0=makeQuery(id+"F7.opExtrude","SWEPT_BODY",BODY,{"disambiguationData":[OSD([sQuery(id+"F6.wireOp",EDGE,"E21.bottom"),sQuery(id+"F6.wireOp",EDGE,"E21.top"),sQuery(id+"F6.wireOp",EDGE,"E21.left"),sQuery(id+"F6.wireOp",EDGE,"E27")])]});
            var Q1;
            Q1=makeQuery(id+"F5.opExtrude","SWEPT_BODY",BODY,{"disambiguationData":[OSD([sQuery(id+"F4.wireOp",EDGE,"E14.bottom"),sQuery(id+"F4.wireOp",EDGE,"E14.top"),sQuery(id+"F4.wireOp",EDGE,"E14.left"),sQuery(id+"F4.wireOp",EDGE,"E20")])]});
            var Q2;
            Q2=makeQuery(id+"F1.opExtrude","SWEPT_BODY",BODY,{"disambiguationData":[OSD([sQuery(id+"F0.wireOp",EDGE,"E1.bottom"),sQuery(id+"F0.wireOp",EDGE,"E1.top"),sQuery(id+"F0.wireOp",EDGE,"E1.left"),sQuery(id+"F0.wireOp",EDGE,"E1.right"),sQuery(id+"F0.wireOp",EDGE,"E3"),sQuery(id+"F0.wireOp",EDGE,"E4")])]});
            var Q3;
            Q3=makeQuery(id+"F3.opExtrude","SWEPT_BODY",BODY,{"disambiguationData":[OSD([sQuery(id+"F2.wireOp",EDGE,"E8.bottom"),sQuery(id+"F2.wireOp",EDGE,"E8.top"),sQuery(id+"F2.wireOp",EDGE,"E8.right"),sQuery(id+"F2.wireOp",EDGE,"E13")])]});
            var Q4;
            Q4=makeQuery(id+"F9.opExtrude","SWEPT_BODY",BODY,{"disambiguationData":[OSD([sQuery(id+"F8.wireOp",EDGE,"E29.bottom"),sQuery(id+"F8.wireOp",EDGE,"E29.top"),sQuery(id+"F8.wireOp",EDGE,"E29.right"),sQuery(id+"F8.wireOp",EDGE,"E34")])]});
            booleanBodies(context, id + "F14", {"operationType" : BooleanOperationType.UNION, "tools" : qUnion([Q0, Q1, Q2, Q3, Q4])});
        }
        {
            var Q0;
            Q0=makeQuery(id+"F14.opBoolean","MERGE",FACE,{"derivedFrom":[makeQuery(id+"F1.opExtrude","SWEPT_FACE",FACE,{"disambiguationData":[OSD([sQuery(id+"F0.wireOp",EDGE,"E1.bottom")])]}),makeQuery(id+"F3.opExtrude","SWEPT_FACE",FACE,{"disambiguationData":[OSD([sQuery(id+"F2.wireOp",EDGE,"E8.bottom")])]}),makeQuery(id+"F5.opExtrude","SWEPT_FACE",FACE,{"disambiguationData":[OSD([sQuery(id+"F4.wireOp",EDGE,"E14.top")])]}),makeQuery(id+"F7.opExtrude","SWEPT_FACE",FACE,{"disambiguationData":[OSD([sQuery(id+"F6.wireOp",EDGE,"E21.top")])]}),makeQuery(id+"F9.opExtrude","SWEPT_FACE",FACE,{"disambiguationData":[OSD([sQuery(id+"F8.wireOp",EDGE,"E29.bottom")])]})]});
            var sketch = newSketch(context, id + "F15", { "sketchPlane" : qUnion([Q0])});
            skCircle(sketch, "E35", {"center": v(33, 9) * mm, "radius": 2.75 * mm});
            skLineSegment(sketch, "E36", {"start": v(33, 9) * mm, "end": v(33, -9) * mm, "construction": true});
            skCircle(sketch, "E37", {"center": v(33, -9) * mm, "radius": 2.75 * mm});
            skLineSegment(sketch, "E38", {"start": v(33, -9) * mm, "end": v(9, -9) * mm, "construction": true});
            skCircle(sketch, "E39", {"center": v(9, -9) * mm, "radius": 2.75 * mm});
            skLineSegment(sketch, "E40", {"start": v(9, -9) * mm, "end": v(9, 9) * mm, "construction": true});
            skLineSegment(sketch, "E41", {"start": v(33, 9) * mm, "end": v(9, 9) * mm, "construction": true});
            skCircle(sketch, "E42", {"center": v(9, 9) * mm, "radius": 2.75 * mm});
            skSolve(sketch);
        }
        {
            var Q0;
            Q0=makeQuery(id+"F15.imprint","IMPRINT",FACE,{"disambiguationData":[TD([[makeQuery(id+"F15.imprint","IMPRINT",EDGE,{"derivedFrom":sQuery(id+"F15.wireOp",EDGE,"E35")}),1.0]])]});
            var Q1;
            Q1=makeQuery(id+"F15.imprint","IMPRINT",FACE,{"disambiguationData":[TD([[makeQuery(id+"F15.imprint","IMPRINT",EDGE,{"derivedFrom":sQuery(id+"F15.wireOp",EDGE,"E37")}),1.0]])]});
            var Q2;
            Q2=makeQuery(id+"F15.imprint","IMPRINT",FACE,{"disambiguationData":[TD([[makeQuery(id+"F15.imprint","IMPRINT",EDGE,{"derivedFrom":sQuery(id+"F15.wireOp",EDGE,"9YfTtbZ8-3puh-lQBR-agRP-eiKW6LKNhFDY")}),1.0]])]});
            var Q3;
            Q3=makeQuery(id+"F15.imprint","IMPRINT",FACE,{"disambiguationData":[TD([[makeQuery(id+"F15.imprint","IMPRINT",EDGE,{"derivedFrom":sQuery(id+"F15.wireOp",EDGE,"E39")}),1.0]])]});
            var Q4;
            Q4=makeQuery(id+"F15.imprint","IMPRINT",FACE,{"disambiguationData":[TD([[makeQuery(id+"F15.imprint","IMPRINT",EDGE,{"derivedFrom":sQuery(id+"F15.wireOp",EDGE,"E42")}),1.0]])]});
            var Q5;
            Q5=makeQuery(id+"F14.opBoolean","MERGE",FACE,{"derivedFrom":[makeQuery(id+"F1.opExtrude","SWEPT_FACE",FACE,{"disambiguationData":[OSD([sQuery(id+"F0.wireOp",EDGE,"E1.top")])]}),makeQuery(id+"F3.opExtrude","SWEPT_FACE",FACE,{"disambiguationData":[OSD([sQuery(id+"F2.wireOp",EDGE,"E8.top")])]}),makeQuery(id+"F5.opExtrude","SWEPT_FACE",FACE,{"disambiguationData":[OSD([sQuery(id+"F4.wireOp",EDGE,"E14.bottom")])]}),makeQuery(id+"F7.opExtrude","SWEPT_FACE",FACE,{"disambiguationData":[OSD([sQuery(id+"F6.wireOp",EDGE,"E21.bottom")])]}),makeQuery(id+"F9.opExtrude","SWEPT_FACE",FACE,{"disambiguationData":[OSD([sQuery(id+"F8.wireOp",EDGE,"E29.top")])]})]});
            extrude(context, id + "F16", {"entities" : qUnion([Q0, Q1, Q2, Q3, Q4]), "operationType" : NewBodyOperationType.REMOVE, "endBound" : BoundingType.UP_TO_SURFACE, "oppositeDirection" : true, "depth" : 25 * mm, "endBoundEntityFace" : qUnion([Q5]), "offsetDistance" : 25 * mm});
        }
        {
            var Q0;
            Q0=makeQuery(id+"F14.opBoolean","MERGE",FACE,{"derivedFrom":[makeQuery(id+"F1.opExtrude","SWEPT_FACE",FACE,{"disambiguationData":[OSD([sQuery(id+"F0.wireOp",EDGE,"E1.bottom")])]}),makeQuery(id+"F3.opExtrude","SWEPT_FACE",FACE,{"disambiguationData":[OSD([sQuery(id+"F2.wireOp",EDGE,"E8.bottom")])]}),makeQuery(id+"F5.opExtrude","SWEPT_FACE",FACE,{"disambiguationData":[OSD([sQuery(id+"F4.wireOp",EDGE,"E14.top")])]}),makeQuery(id+"F7.opExtrude","SWEPT_FACE",FACE,{"disambiguationData":[OSD([sQuery(id+"F6.wireOp",EDGE,"E21.top")])]}),makeQuery(id+"F9.opExtrude","SWEPT_FACE",FACE,{"disambiguationData":[OSD([sQuery(id+"F8.wireOp",EDGE,"E29.bottom")])]})]});
            var sketch = newSketch(context, id + "F17", { "sketchPlane" : qUnion([Q0])});
            skCircle(sketch, "E43", {"center": v(33, -9) * mm, "radius": 4.5 * mm});
            skCircle(sketch, "E44", {"center": v(33, 9) * mm, "radius": 4.5 * mm});
            skSolve(sketch);
        }
        {
            var Q0;
            Q0 = qSketchRegion(id + "F17", true);
            extrude(context, id + "F18", {"entities" : qUnion([Q0]), "operationType" : NewBodyOperationType.REMOVE, "oppositeDirection" : true, "depth" : 3 * mm, "offsetDistance" : 25 * mm});
        }
        {
            var Q0;
            Q0=makeQuery(id+"F13.opBoolean","MERGE",FACE,{"derivedFrom":[makeQuery(id+"F9.opExtrude","SWEPT_FACE",FACE,{"disambiguationData":[OSD([sQuery(id+"F8.wireOp",EDGE,"E28.top")])]}),makeQuery(id+"F12.opBoolean","MERGE",FACE,{"derivedFrom":[makeQuery(id+"F3.opExtrude","SWEPT_FACE",FACE,{"disambiguationData":[OSD([sQuery(id+"F2.wireOp",EDGE,"E7.top")])]}),makeQuery(id+"F11.opBoolean","MERGE",FACE,{"derivedFrom":[makeQuery(id+"F1.opExtrude","SWEPT_FACE",FACE,{"disambiguationData":[OSD([sQuery(id+"F0.wireOp",EDGE,"E0.top")])]}),makeQuery(id+"F10.opBoolean","MERGE",FACE,{"derivedFrom":[makeQuery(id+"F5.opExtrude","SWEPT_FACE",FACE,{"disambiguationData":[OSD([sQuery(id+"F4.wireOp",EDGE,"E15.bottom")])]}),makeQuery(id+"F7.opExtrude","SWEPT_FACE",FACE,{"disambiguationData":[OSD([sQuery(id+"F6.wireOp",EDGE,"E22.bottom")])]})]})]})]})]});
            var sketch = newSketch(context, id + "F19", { "sketchPlane" : qUnion([Q0])});
            skCircle(sketch, "E45", {"center": v(9, -9) * mm, "radius": 4.5 * mm});
            skCircle(sketch, "E46", {"center": v(9, 9) * mm, "radius": 4.5 * mm});
            skSolve(sketch);
        }
        {
            var Q0;
            Q0 = qSketchRegion(id + "F19", true);
            extrude(context, id + "F20", {"entities" : qUnion([Q0]), "operationType" : NewBodyOperationType.REMOVE, "oppositeDirection" : true, "depth" : 3 * mm, "offsetDistance" : 25 * mm});
        }
        {
            var Q0;
            Q0=makeQuery(id+"F13.opBoolean","MERGE",EDGE,{"derivedFrom":[makeQuery(id+"F9.opExtrude","SWEPT_EDGE",EDGE,{"disambiguationData":[OSD([sQuery(id+"F8.wireOp",EDGE,"E28.top"),sQuery(id+"F8.wireOp",EDGE,"E28.left")])]}),makeQuery(id+"F12.opBoolean","MERGE",EDGE,{"derivedFrom":[makeQuery(id+"F3.opExtrude","SWEPT_EDGE",EDGE,{"disambiguationData":[OSD([sQuery(id+"F2.wireOp",EDGE,"E7.top"),sQuery(id+"F2.wireOp",EDGE,"E7.left")])]}),makeQuery(id+"F11.opBoolean","MERGE",EDGE,{"derivedFrom":[makeQuery(id+"F1.opExtrude","SWEPT_EDGE",EDGE,{"disambiguationData":[OSD([sQuery(id+"F0.wireOp",EDGE,"E0.top"),sQuery(id+"F0.wireOp",EDGE,"E0.left")])]}),makeQuery(id+"F10.opBoolean","MERGE",EDGE,{"derivedFrom":[makeQuery(id+"F5.opExtrude","SWEPT_EDGE",EDGE,{"disambiguationData":[OSD([sQuery(id+"F4.wireOp",EDGE,"E15.bottom"),sQuery(id+"F4.wireOp",EDGE,"E15.right")])]}),makeQuery(id+"F7.opExtrude","SWEPT_EDGE",EDGE,{"disambiguationData":[OSD([sQuery(id+"F6.wireOp",EDGE,"E22.bottom"),sQuery(id+"F6.wireOp",EDGE,"E22.right")])]})]})]})]})]});
            var Q1;
            Q1=makeQuery(id+"F7.opExtrude","CAP_EDGE",EDGE,{"disambiguationData":[OSD([sQuery(id+"F6.wireOp",EDGE,"E22.bottom")])],"isStart":false});
            var Q2;
            Q2=makeQuery(id+"F9.opExtrude","CAP_EDGE",EDGE,{"disambiguationData":[OSD([sQuery(id+"F8.wireOp",EDGE,"E28.top")])],"isStart":false});
            var Q3;
            Q3=makeQuery(id+"F7.opExtrude","CAP_EDGE",EDGE,{"disambiguationData":[OSD([sQuery(id+"F6.wireOp",EDGE,"E21.top")])],"isStart":false});
            var Q4;
            Q4=makeQuery(id+"F14.opBoolean","MERGE",EDGE,{"derivedFrom":[makeQuery(id+"F1.opExtrude","SWEPT_EDGE",EDGE,{"disambiguationData":[OSD([sQuery(id+"F0.wireOp",EDGE,"E1.bottom"),sQuery(id+"F0.wireOp",EDGE,"E1.right")])]}),makeQuery(id+"F3.opExtrude","SWEPT_EDGE",EDGE,{"disambiguationData":[OSD([sQuery(id+"F2.wireOp",EDGE,"E8.bottom"),sQuery(id+"F2.wireOp",EDGE,"E8.right")])]}),makeQuery(id+"F5.opExtrude","SWEPT_EDGE",EDGE,{"disambiguationData":[OSD([sQuery(id+"F4.wireOp",EDGE,"E14.top"),sQuery(id+"F4.wireOp",EDGE,"E14.left")])]}),makeQuery(id+"F7.opExtrude","SWEPT_EDGE",EDGE,{"disambiguationData":[OSD([sQuery(id+"F6.wireOp",EDGE,"E21.top"),sQuery(id+"F6.wireOp",EDGE,"E21.left")])]}),makeQuery(id+"F9.opExtrude","SWEPT_EDGE",EDGE,{"disambiguationData":[OSD([sQuery(id+"F8.wireOp",EDGE,"E29.bottom"),sQuery(id+"F8.wireOp",EDGE,"E29.right")])]})]});
            var Q5;
            Q5=makeQuery(id+"F9.opExtrude","CAP_EDGE",EDGE,{"disambiguationData":[OSD([sQuery(id+"F8.wireOp",EDGE,"E29.bottom")])],"isStart":false});
            chamfer(context, id + "F21", {"entities" : qUnion([Q0, Q1, Q2, Q3, Q4, Q5]), "width" : 2 * mm, "tangentPropagation" : true});
        }
        {
            var Q0;
            Q0=makeQuery(id+"F7.opExtrude","CAP_EDGE",EDGE,{"disambiguationData":[OSD([sQuery(id+"F6.wireOp",EDGE,"E24")])],"isStart":false});
            var Q1;
            Q1=makeQuery(id+"F9.opExtrude","CAP_EDGE",EDGE,{"disambiguationData":[OSD([sQuery(id+"F8.wireOp",EDGE,"E31")])],"isStart":false});
            var Q2;
            Q2=makeQuery(id+"F7.opExtrude","CAP_EDGE",EDGE,{"disambiguationData":[OSD([sQuery(id+"F6.wireOp",EDGE,"E27")])],"isStart":false});
            var Q3;
            Q3=makeQuery(id+"F9.opExtrude","CAP_EDGE",EDGE,{"disambiguationData":[OSD([sQuery(id+"F8.wireOp",EDGE,"E34")])],"isStart":false});
            chamfer(context, id + "F22", {"entities" : qUnion([Q0, Q1, Q2, Q3]), "width" : 1 * mm, "tangentPropagation" : true});
        }
        {
            var Q0;
            Q0=makeQuery(id+"F14.opBoolean","MERGE",EDGE,{"derivedFrom":[makeQuery(id+"F3.opExtrude","SWEPT_EDGE",EDGE,{"disambiguationData":[OSD([sQuery(id+"F2.wireOp",EDGE,"E8.top"),sQuery(id+"F2.wireOp",EDGE,"E13")])]}),makeQuery(id+"F9.opExtrude","SWEPT_EDGE",EDGE,{"disambiguationData":[OSD([sQuery(id+"F8.wireOp",EDGE,"E29.top"),sQuery(id+"F8.wireOp",EDGE,"E34")])]})]});
            var Q1;
            Q1=makeQuery(id+"F12.opBoolean","MERGE",EDGE,{"derivedFrom":[makeQuery(id+"F3.opExtrude","SWEPT_EDGE",EDGE,{"disambiguationData":[OSD([sQuery(id+"F2.wireOp",EDGE,"E7.bottom"),sQuery(id+"F2.wireOp",EDGE,"E13")])]}),makeQuery(id+"F11.opBoolean","MERGE",EDGE,{"derivedFrom":[makeQuery(id+"F1.opExtrude","SWEPT_EDGE",EDGE,{"disambiguationData":[OSD([sQuery(id+"F0.wireOp",EDGE,"E0.bottom"),sQuery(id+"F0.wireOp",EDGE,"E6")])]}),makeQuery(id+"F5.opExtrude","SWEPT_EDGE",EDGE,{"disambiguationData":[OSD([sQuery(id+"F4.wireOp",EDGE,"E15.top"),sQuery(id+"F4.wireOp",EDGE,"E20")])]})]})]});
            var Q2;
            Q2=makeQuery(id+"F14.opBoolean","MERGE",EDGE,{"derivedFrom":[makeQuery(id+"F5.opExtrude","SWEPT_EDGE",EDGE,{"disambiguationData":[OSD([sQuery(id+"F4.wireOp",EDGE,"E14.bottom"),sQuery(id+"F4.wireOp",EDGE,"E20")])]}),makeQuery(id+"F7.opExtrude","SWEPT_EDGE",EDGE,{"disambiguationData":[OSD([sQuery(id+"F6.wireOp",EDGE,"E21.bottom"),sQuery(id+"F6.wireOp",EDGE,"E27")])]})]});
            chamfer(context, id + "F23", {"entities" : qUnion([Q0, Q1, Q2]), "width" : 2 * mm, "tangentPropagation" : true});
        }
    });
